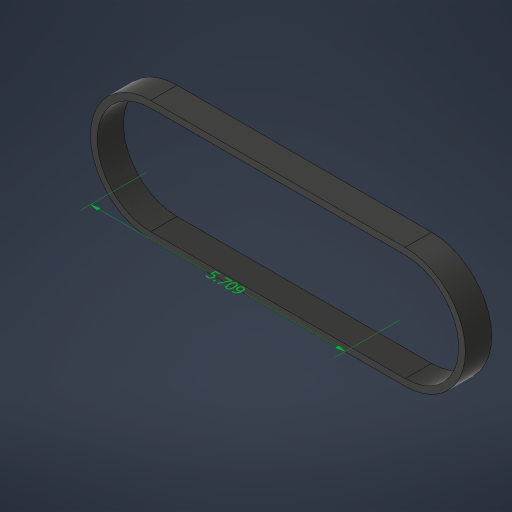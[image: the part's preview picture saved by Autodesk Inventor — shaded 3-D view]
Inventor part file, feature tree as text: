
AUTODESK INVENTOR PART (.ipt)
format: ipt  version: 2023.1 (Build 271208000, 208)  size: 224,256 bytes
history: native  units: in
note: dims shown in document units (in); Inventor stores cm internally (conversion verified against a paired STEP export)
features: other x4, extrude x1, projected_geometry x1
ambient origin geometry x8: Origin, YZ Plane, XZ Plane, XY Plane, X Axis, Y Axis, Z Axis, Center Point
bodies: Body1 (feature_tree)
feature tree (6):
  other  "Annotations"
  extrude  "BeltInternalAreaCut"  TaperAngle=0.0deg  [1 undecoded]
  other  "BeltOuterProfile"
  other  "BeltThickness"
  projected_geometry  "Projected Loop1"
  other  "Linear Dimension 1"
note: 1 required parameter value undecoded (feature->parameter linkage not recoverable at this tier; creation-order binding heuristic only, values carry confidence <= 0.55)
